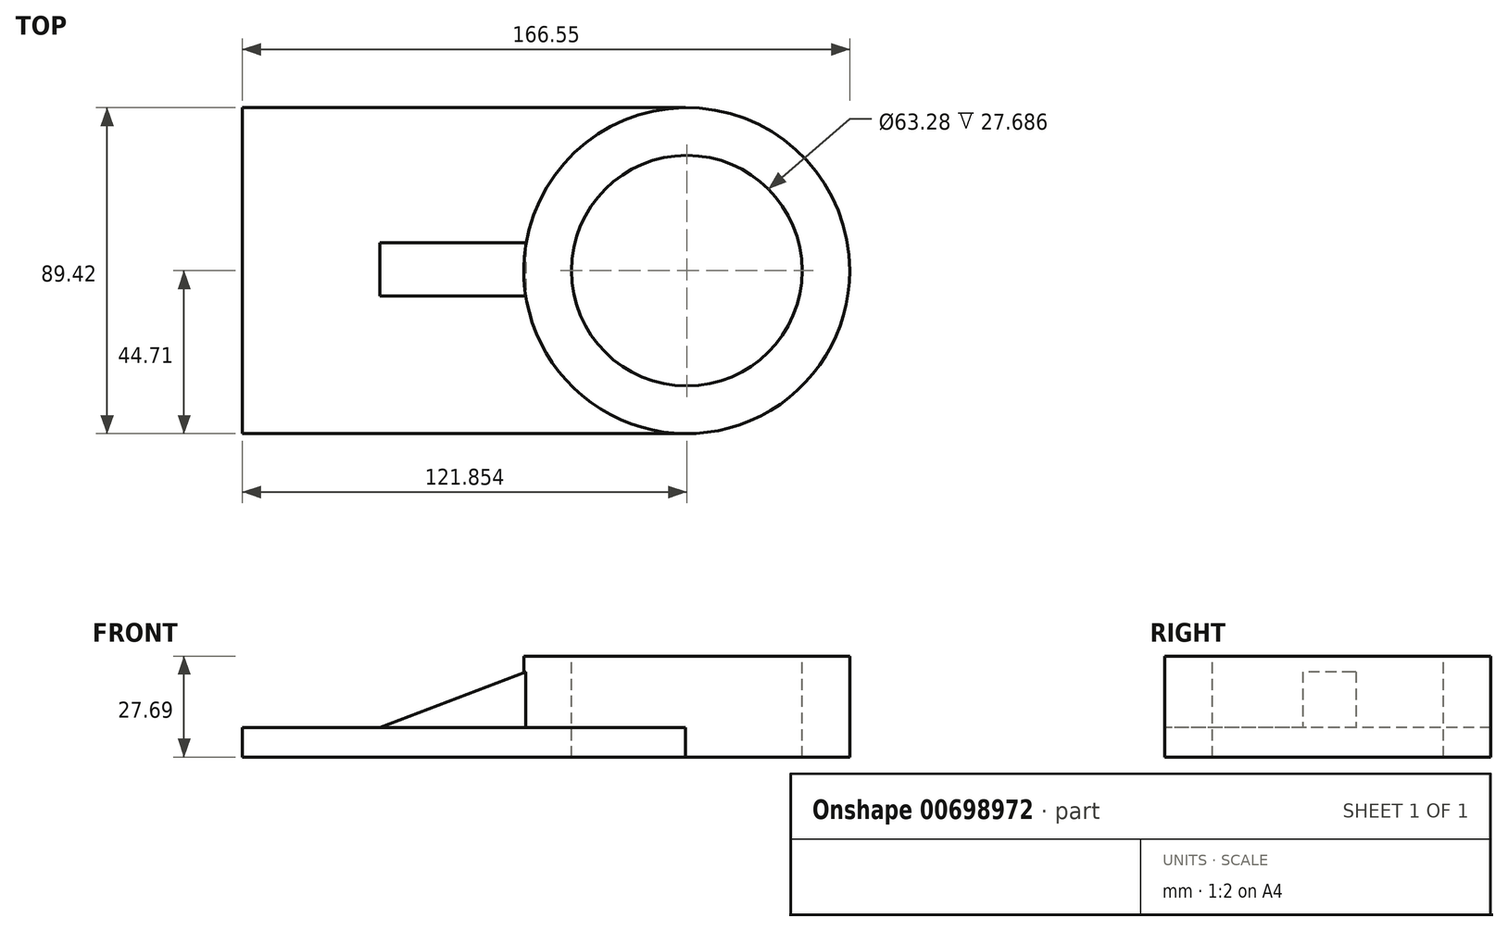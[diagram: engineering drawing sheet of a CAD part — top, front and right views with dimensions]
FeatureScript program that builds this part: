
annotation { "Feature Type Name" : "Feature", "Feature Type Description" : "" }
export const myFeature = defineFeature(function(context is Context, id is Id, definition is map)
    precondition{}
    {
        {
            var Q0;
            Q0=qCreatedBy(makeId("Top.planeOp"),FACE);
            var sketch = newSketch(context, id + "F0", { "sketchPlane" : qUnion([Q0])});
            skLineSegment(sketch, "E0.bottom", {"start": v(-60.74, 44.7) * mm, "end": v(60.74, 44.7) * mm});
            skLineSegment(sketch, "E0.top", {"start": v(-60.74, -44.7) * mm, "end": v(60.74, -44.7) * mm});
            skLineSegment(sketch, "E0.left", {"start": v(-60.74, 44.7) * mm, "end": v(-60.74, -44.7) * mm});
            skLineSegment(sketch, "E0.right", {"start": v(60.74, 44.7) * mm, "end": v(60.74, -44.7) * mm});
            skPoint(sketch, "E0.middle", {"position": v(0, 0) * mm});
            skSolve(sketch);
        }
        {
            var Q0;
            Q0 = qSketchRegion(id + "F0", true);
            extrude(context, id + "F1", {"entities" : qUnion([Q0]), "depth" : 8.13 * mm, "offsetDistance" : 25.4 * mm});
        }
        {
            var Q0;
            Q0=qCreatedBy(makeId("Top.planeOp"),FACE);
            var sketch = newSketch(context, id + "F2", { "sketchPlane" : qUnion([Q0])});
            skCircle(sketch, "E1", {"center": v(61.11, 0) * mm, "radius": 44.7 * mm});
            skSolve(sketch);
        }
        {
            var Q0;
            Q0=makeQuery(id+"F2.imprint","IMPRINT",FACE,{"disambiguationData":[TD([[makeQuery(id+"F2.imprint","IMPRINT",EDGE,{"derivedFrom":sQuery(id+"F2.wireOp",EDGE,"E1")}),1.0]])]});
            extrude(context, id + "F3", {"entities" : qUnion([Q0]), "operationType" : NewBodyOperationType.ADD, "depth" : 27.7 * mm, "offsetDistance" : 25.4 * mm});
        }
        {
            var Q0;
            Q0=makeQuery(id+"F3.opExtrude","CAP_FACE",FACE,{"disambiguationData":[OSD([sQuery(id+"F2.wireOp",EDGE,"E1")])],"isStart":false});
            var sketch = newSketch(context, id + "F4", { "sketchPlane" : qUnion([Q0])});
            skCircle(sketch, "E2", {"center": v(61.11, 0) * mm, "radius": 31.64 * mm});
            skSolve(sketch);
        }
        {
            var Q0;
            Q0=makeQuery(id+"F4.imprint","IMPRINT",FACE,{"disambiguationData":[TD([[makeQuery(id+"F4.imprint","IMPRINT",EDGE,{"derivedFrom":sQuery(id+"F4.wireOp",EDGE,"E2")}),1.0]])]});
            extrude(context, id + "F5", {"entities" : qUnion([Q0]), "operationType" : NewBodyOperationType.REMOVE, "oppositeDirection" : true, "depth" : 71.12 * mm, "offsetDistance" : 25.4 * mm});
        }
        {
            var Q0;
            Q0=makeQuery(id+"F1.opExtrude","CAP_FACE",FACE,{"disambiguationData":[OSD([sQuery(id+"F0.wireOp",EDGE,"E0.bottom"),sQuery(id+"F0.wireOp",EDGE,"E0.top"),sQuery(id+"F0.wireOp",EDGE,"E0.left"),sQuery(id+"F0.wireOp",EDGE,"E0.right")])],"isStart":false});
            var sketch = newSketch(context, id + "F6", { "sketchPlane" : qUnion([Q0])});
            skLineSegment(sketch, "E3.bottom", {"start": v(17.32, 8.92) * mm, "end": v(-15.37, 8.92) * mm});
            skLineSegment(sketch, "E3.top", {"start": v(17.32, -5.97) * mm, "end": v(-15.37, -5.97) * mm});
            skLineSegment(sketch, "E3.left", {"start": v(17.32, 8.92) * mm, "end": v(17.32, -5.97) * mm});
            skLineSegment(sketch, "E3.right", {"start": v(-15.37, 8.92) * mm, "end": v(-15.37, -5.97) * mm});
            skSolve(sketch);
        }
        {
            var Q0;
            {var subQ0=sQuery(id+"F6.wireOp",EDGE,"E3.left");Q0=makeQuery(id+"F6.imprint","IMPRINT",FACE,{"disambiguationData":[TD([[makeQuery(id+"F6.imprint","IMPRINT",EDGE,{"derivedFrom":subQ0}),-1.0]])]});}
            extrude(context, id + "F7", {"entities" : qUnion([Q0]), "operationType" : NewBodyOperationType.ADD, "depth" : 12.7 * mm, "offsetDistance" : 25.4 * mm});
        }
        {
            var Q0;
            Q0=makeQuery(id+"F1.opExtrude","CAP_FACE",FACE,{"disambiguationData":[OSD([sQuery(id+"F0.wireOp",EDGE,"E0.bottom"),sQuery(id+"F0.wireOp",EDGE,"E0.top"),sQuery(id+"F0.wireOp",EDGE,"E0.left"),sQuery(id+"F0.wireOp",EDGE,"E0.right")])],"isStart":false});
            var sketch = newSketch(context, id + "F8", { "sketchPlane" : qUnion([Q0])});
            skLineSegment(sketch, "E4.bottom", {"start": v(17.07, 7.63) * mm, "end": v(-23.08, 7.63) * mm});
            skLineSegment(sketch, "E4.top", {"start": v(17.07, -6.91) * mm, "end": v(-23.08, -6.91) * mm});
            skLineSegment(sketch, "E4.left", {"start": v(17.07, 7.63) * mm, "end": v(17.07, -6.91) * mm});
            skLineSegment(sketch, "E4.right", {"start": v(-23.08, 7.63) * mm, "end": v(-23.08, -6.91) * mm});
            skSolve(sketch);
        }
        {
            var Q0;
            {var subQ0=sQuery(id+"F8.wireOp",EDGE,"E4.bottom");Q0=makeQuery(id+"F8.imprint","IMPRINT",FACE,{"disambiguationData":[TD([[makeQuery(id+"F8.imprint","IMPRINT",EDGE,{"derivedFrom":subQ0}),1.0]])]});}
            extrude(context, id + "F9", {"entities" : qUnion([Q0]), "operationType" : NewBodyOperationType.ADD, "depth" : 15.24 * mm, "offsetDistance" : 25.4 * mm});
        }
        {
            var Q0;
            Q0=makeQuery(id+"F9.opExtrude","SWEPT_FACE",FACE,{"disambiguationData":[OSD([sQuery(id+"F8.wireOp",EDGE,"E4.top")])]});
            var sketch = newSketch(context, id + "F10", { "sketchPlane" : qUnion([Q0])});
            skLineSegment(sketch, "E5", {"start": v(-23.08, 8.13) * mm, "end": v(16.95, 23.37) * mm});
            skSolve(sketch);
        }
        {
            var Q0;
            Q0=makeQuery(id+"F10.imprint","IMPRINT",FACE,{"disambiguationData":[TD([[makeQuery(id+"F10.imprint","IMPRINT",EDGE,{"derivedFrom":sQuery(id+"F10.wireOp",EDGE,"E5")}),1.0]])]});
            extrude(context, id + "F11", {"entities" : qUnion([Q0]), "operationType" : NewBodyOperationType.REMOVE, "oppositeDirection" : true, "depth" : 25.4 * mm, "offsetDistance" : 25.4 * mm});
        }
    });
